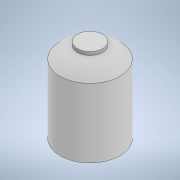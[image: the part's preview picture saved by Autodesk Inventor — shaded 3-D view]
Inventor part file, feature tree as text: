
AUTODESK INVENTOR PART (.ipt)
format: ipt  version: 2022 (Build 260153000, 153)  size: 114,176 bytes
history: native  units: in
note: dims shown in document units (in); Inventor stores cm internally (conversion verified against a paired STEP export)
features: revolve x1, sketch x1
ambient origin geometry x8: Origin, YZ Plane, XZ Plane, XY Plane, X Axis, Y Axis, Z Axis, Center Point
bodies: Solid1 (feature_tree)
feature tree (2):
  revolve  "Revolution1"  [1 undecoded]
  sketch  "Sketch1"  dims[d0=43.0in d1=49.48in d2=18.0in d3=2.34in d4=28.11in d5=360.0deg]
note: 1 required parameter value undecoded (feature->parameter linkage not recoverable at this tier; creation-order binding heuristic only, values carry confidence <= 0.55)
